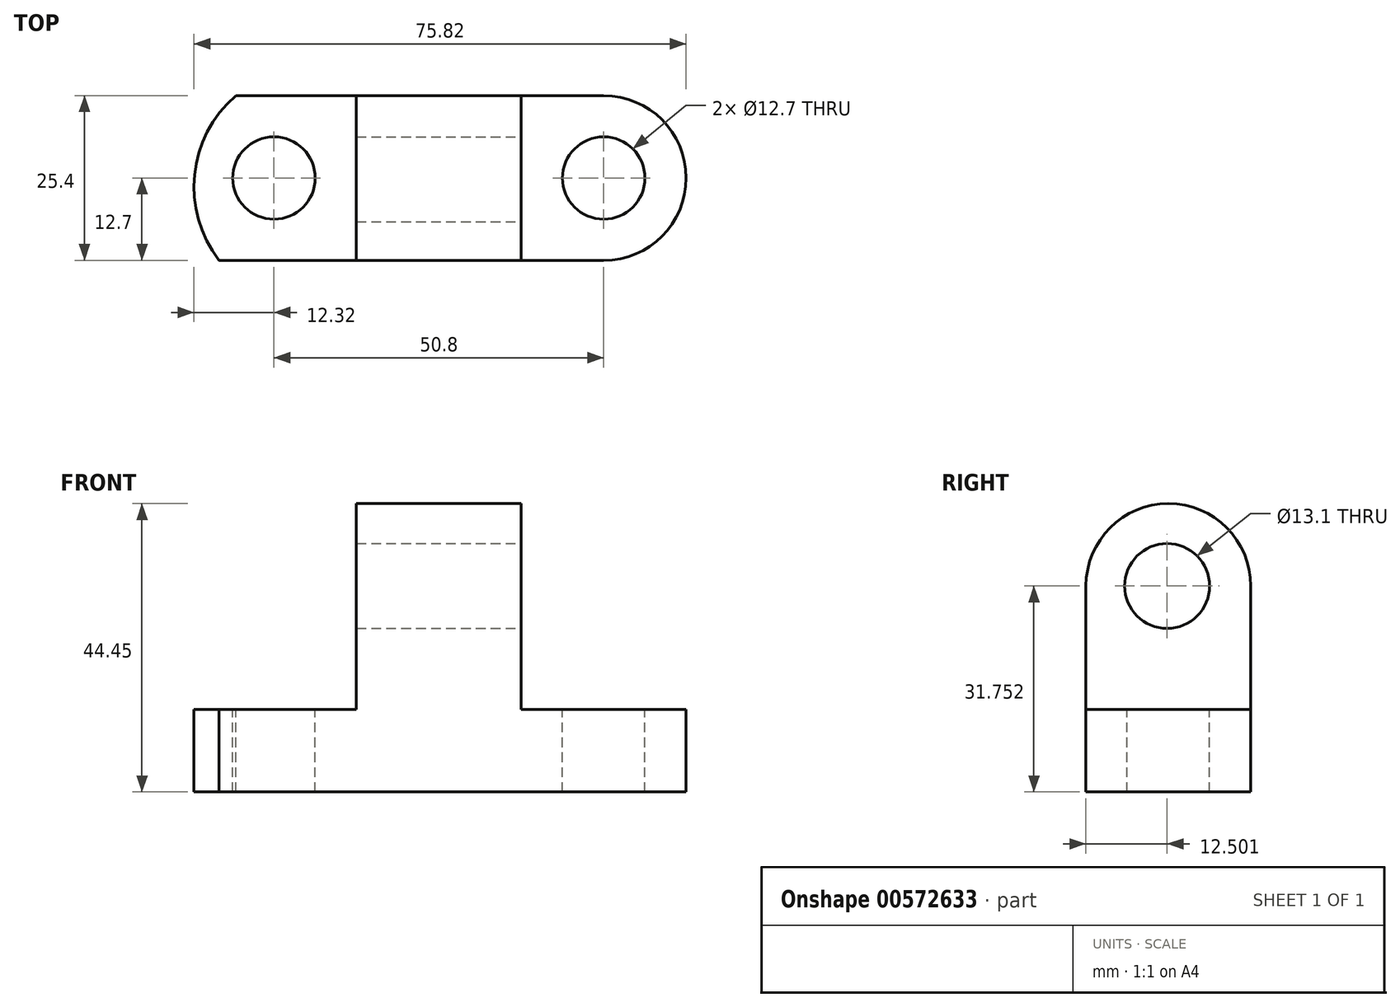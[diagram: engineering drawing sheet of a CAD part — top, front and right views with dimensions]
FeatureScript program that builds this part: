
annotation { "Feature Type Name" : "Feature", "Feature Type Description" : "" }
export const myFeature = defineFeature(function(context is Context, id is Id, definition is map)
    precondition{}
    {
        {
            var Q0;
            Q0=qCreatedBy(makeId("Front.planeOp"),FACE);
            var sketch = newSketch(context, id + "F0", { "sketchPlane" : qUnion([Q0])});
            skLineSegment(sketch, "E0", {"start": v(0, 0) * mm, "end": v(76.2, 0) * mm});
            skLineSegment(sketch, "E1", {"start": v(76.2, 0) * mm, "end": v(76.2, 44.45) * mm});
            skLineSegment(sketch, "E2", {"start": v(76.2, 44.45) * mm, "end": v(0, 44.45) * mm});
            skLineSegment(sketch, "E3", {"start": v(0, 44.45) * mm, "end": v(0, 0) * mm});
            skSolve(sketch);
        }
        {
            var Q0;
            Q0=makeQuery(id+"F0.imprint","IMPRINT",FACE,{"disambiguationData":[TD([[makeQuery(id+"F0.imprint","IMPRINT",EDGE,{"derivedFrom":sQuery(id+"F0.wireOp",EDGE,"E0")}),1.0]])]});
            extrude(context, id + "F1", {"entities" : qUnion([Q0]), "depth" : 25.4 * mm, "offsetDistance" : 25.4 * mm});
        }
        {
            var Q0;
            Q0=makeQuery(id+"F1.opExtrude","CAP_FACE",FACE,{"disambiguationData":[OSD([sQuery(id+"F0.wireOp",EDGE,"E0"),sQuery(id+"F0.wireOp",EDGE,"E1"),sQuery(id+"F0.wireOp",EDGE,"E2"),sQuery(id+"F0.wireOp",EDGE,"E3")])],"isStart":false});
            var sketch = newSketch(context, id + "F2", { "sketchPlane" : qUnion([Q0])});
            skLineSegment(sketch, "E4", {"start": v(0, 0) * mm, "end": v(25.4, 0) * mm});
            skLineSegment(sketch, "E5", {"start": v(25.4, 12.7) * mm, "end": v(25.4, 44.45) * mm});
            skLineSegment(sketch, "E6", {"start": v(25.4, 44.45) * mm, "end": v(50.8, 44.45) * mm});
            skLineSegment(sketch, "E7", {"start": v(50.8, 44.45) * mm, "end": v(50.8, 12.7) * mm});
            skLineSegment(sketch, "E8", {"start": v(50.8, 0) * mm, "end": v(76.2, 0) * mm});
            skLineSegment(sketch, "E9", {"start": v(50.8, 12.7) * mm, "end": v(76.2, 12.7) * mm});
            skLineSegment(sketch, "E10", {"start": v(25.4, 12.7) * mm, "end": v(0, 12.7) * mm});
            skSolve(sketch);
        }
        {
            var Q0;
            {var subQ0=sQuery(id+"F2.wireOp",EDGE,"E7");Q0=makeQuery(id+"F2.imprint","IMPRINT",FACE,{"disambiguationData":[TD([[makeQuery(id+"F2.imprint","IMPRINT",EDGE,{"derivedFrom":subQ0}),1.0]])]});}
            var Q1;
            {var subQ0=sQuery(id+"F2.wireOp",EDGE,"E5");Q1=makeQuery(id+"F2.imprint","IMPRINT",FACE,{"disambiguationData":[TD([[makeQuery(id+"F2.imprint","IMPRINT",EDGE,{"derivedFrom":subQ0}),1.0]])]});}
            extrude(context, id + "F3", {"entities" : qUnion([Q0, Q1]), "operationType" : NewBodyOperationType.REMOVE, "oppositeDirection" : true, "depth" : 25.4 * mm, "offsetDistance" : 25.4 * mm});
        }
        {
            var Q0;
            Q0=makeQuery(id+"F3.boolean.opBoolean","COPY",FACE,{"derivedFrom":makeQuery(id+"F3.opExtrude","SWEPT_FACE",FACE,{"disambiguationData":[OSD([sQuery(id+"F2.wireOp",EDGE,"E7")])]})});
            var sketch = newSketch(context, id + "F4", { "sketchPlane" : qUnion([Q0])});
            skCircle(sketch, "E11", {"center": v(-12.9, 31.75) * mm, "radius": 6.55 * mm});
            skArc(sketch, "E12", {"start": v(0, 31.75) * mm, "mid": v(-12.7, 44.45) * mm, "end": v(-25.4, 31.75) * mm});
            skSolve(sketch);
        }
        {
            var Q0;
            Q0=makeQuery(id+"F4.imprint","IMPRINT",FACE,{"disambiguationData":[TD([[makeQuery(id+"F4.imprint","IMPRINT",EDGE,{"derivedFrom":sQuery(id+"F4.wireOp",EDGE,"E11")}),1.0]])]});
            var Q1;
            {var subQ0=sQuery(id+"F4.wireOp",EDGE,"E12");var subQ1=sQuery(id+"F2.wireOp",EDGE,"E7");var subQ2=makeQuery(id+"F3.boolean.opBoolean","COPY",EDGE,{"derivedFrom":makeQuery(id+"F3.opExtrude","CAP_EDGE",EDGE,{"disambiguationData":[OSD([subQ1])],"isStart":true})});var subQ3=makeQuery(id+"F4.imprint","INTERSECT",VERTEX,{"derivedFrom":[subQ2,subQ0]});Q1=makeQuery(id+"F4.imprint","IMPRINT",FACE,{"disambiguationData":[TD([[makeQuery(id+"F4.imprint","IMPRINT",EDGE,{"disambiguationData":[TD([[subQ3,1.0]])],"derivedFrom":subQ0}),-1.0]])]});}
            var Q2;
            {var subQ0=sQuery(id+"F4.wireOp",EDGE,"E12");var subQ1=sQuery(id+"F2.wireOp",EDGE,"E7");var subQ2=makeQuery(id+"F3.boolean.opBoolean","COPY",EDGE,{"derivedFrom":makeQuery(id+"F3.opExtrude","CAP_EDGE",EDGE,{"disambiguationData":[OSD([subQ1])],"isStart":false})});var subQ3=makeQuery(id+"F4.imprint","INTERSECT",VERTEX,{"derivedFrom":[subQ2,subQ0]});Q2=makeQuery(id+"F4.imprint","IMPRINT",FACE,{"disambiguationData":[TD([[makeQuery(id+"F4.imprint","IMPRINT",EDGE,{"disambiguationData":[TD([[subQ3,-1.0]])],"derivedFrom":subQ0}),-1.0]])]});}
            extrude(context, id + "F5", {"entities" : qUnion([Q0, Q1, Q2]), "operationType" : NewBodyOperationType.REMOVE, "oppositeDirection" : true, "depth" : 25.4 * mm, "offsetDistance" : 25.4 * mm});
        }
        {
            var Q0;
            Q0=makeQuery(id+"F3.boolean.opBoolean","COPY",FACE,{"derivedFrom":makeQuery(id+"F3.opExtrude","SWEPT_FACE",FACE,{"disambiguationData":[OSD([sQuery(id+"F2.wireOp",EDGE,"E9")])]})});
            var sketch = newSketch(context, id + "F6", { "sketchPlane" : qUnion([Q0])});
            skCircle(sketch, "E13", {"center": v(63.5, -12.7) * mm, "radius": 6.35 * mm});
            skPoint(sketch, "E13.centerSnap0", {"position": v(50.8, -12.7) * mm});
            skSolve(sketch);
        }
        {
            var Q0;
            Q0=makeQuery(id+"F6.imprint","IMPRINT",FACE,{"disambiguationData":[TD([[makeQuery(id+"F6.imprint","IMPRINT",EDGE,{"derivedFrom":sQuery(id+"F6.wireOp",EDGE,"E13")}),1.0]])]});
            extrude(context, id + "F7", {"entities" : qUnion([Q0]), "operationType" : NewBodyOperationType.REMOVE, "oppositeDirection" : true, "depth" : 25.4 * mm, "offsetDistance" : 25.4 * mm});
        }
        {
            var Q0;
            Q0=makeQuery(id+"F3.boolean.opBoolean","COPY",FACE,{"derivedFrom":makeQuery(id+"F3.opExtrude","SWEPT_FACE",FACE,{"disambiguationData":[OSD([sQuery(id+"F2.wireOp",EDGE,"E9")])]})});
            var sketch = newSketch(context, id + "F8", { "sketchPlane" : qUnion([Q0])});
            skArc(sketch, "E14", {"start": v(63.5, -25.4) * mm, "mid": v(76.2, -12.7) * mm, "end": v(63.5, 0) * mm});
            skLineSegment(sketch, "E15", {"start": v(63.5, 0) * mm, "end": v(76.2, 0) * mm});
            skLineSegment(sketch, "E16", {"start": v(63.5, -25.4) * mm, "end": v(76.2, -25.4) * mm});
            skSolve(sketch);
        }
        {
            var Q0;
            {var subQ0=sQuery(id+"F8.wireOp",EDGE,"E15");Q0=makeQuery(id+"F8.imprint","IMPRINT",FACE,{"disambiguationData":[TD([[makeQuery(id+"F8.imprint","IMPRINT",EDGE,{"derivedFrom":subQ0}),-1.0]])]});}
            var Q1;
            {var subQ0=sQuery(id+"F8.wireOp",EDGE,"E16");Q1=makeQuery(id+"F8.imprint","IMPRINT",FACE,{"disambiguationData":[TD([[makeQuery(id+"F8.imprint","IMPRINT",EDGE,{"derivedFrom":subQ0}),1.0]])]});}
            extrude(context, id + "F9", {"entities" : qUnion([Q0, Q1]), "operationType" : NewBodyOperationType.REMOVE, "oppositeDirection" : true, "depth" : 25.4 * mm, "offsetDistance" : 25.4 * mm});
        }
        {
            var Q0;
            Q0=makeQuery(id+"F3.boolean.opBoolean","COPY",FACE,{"derivedFrom":makeQuery(id+"F3.opExtrude","SWEPT_FACE",FACE,{"disambiguationData":[OSD([sQuery(id+"F2.wireOp",EDGE,"E10")])]})});
            var sketch = newSketch(context, id + "F10", { "sketchPlane" : qUnion([Q0])});
            skCircle(sketch, "E17", {"center": v(12.7, -12.7) * mm, "radius": 6.35 * mm});
            skPoint(sketch, "E17.centerSnap0", {"position": v(12.7, -25.4) * mm});
            skArc(sketch, "E18", {"start": v(6.8, 0) * mm, "mid": v(0.47, -12.2) * mm, "end": v(4.26, -25.4) * mm});
            skLineSegment(sketch, "E19", {"start": v(6.8, 0) * mm, "end": v(0, 0) * mm});
            skLineSegment(sketch, "E20", {"start": v(4.26, -25.4) * mm, "end": v(0, -25.4) * mm});
            skSolve(sketch);
        }
        {
            var Q0;
            Q0=makeQuery(id+"F10.imprint","IMPRINT",FACE,{"disambiguationData":[TD([[makeQuery(id+"F10.imprint","IMPRINT",EDGE,{"derivedFrom":sQuery(id+"F10.wireOp",EDGE,"E18")}),-1.0]])]});
            var Q1;
            Q1=makeQuery(id+"F10.imprint","IMPRINT",FACE,{"disambiguationData":[TD([[makeQuery(id+"F10.imprint","IMPRINT",EDGE,{"derivedFrom":sQuery(id+"F10.wireOp",EDGE,"E17")}),1.0]])]});
            extrude(context, id + "F11", {"entities" : qUnion([Q0, Q1]), "operationType" : NewBodyOperationType.REMOVE, "oppositeDirection" : true, "depth" : 25.4 * mm, "offsetDistance" : 25.4 * mm});
        }
    });
